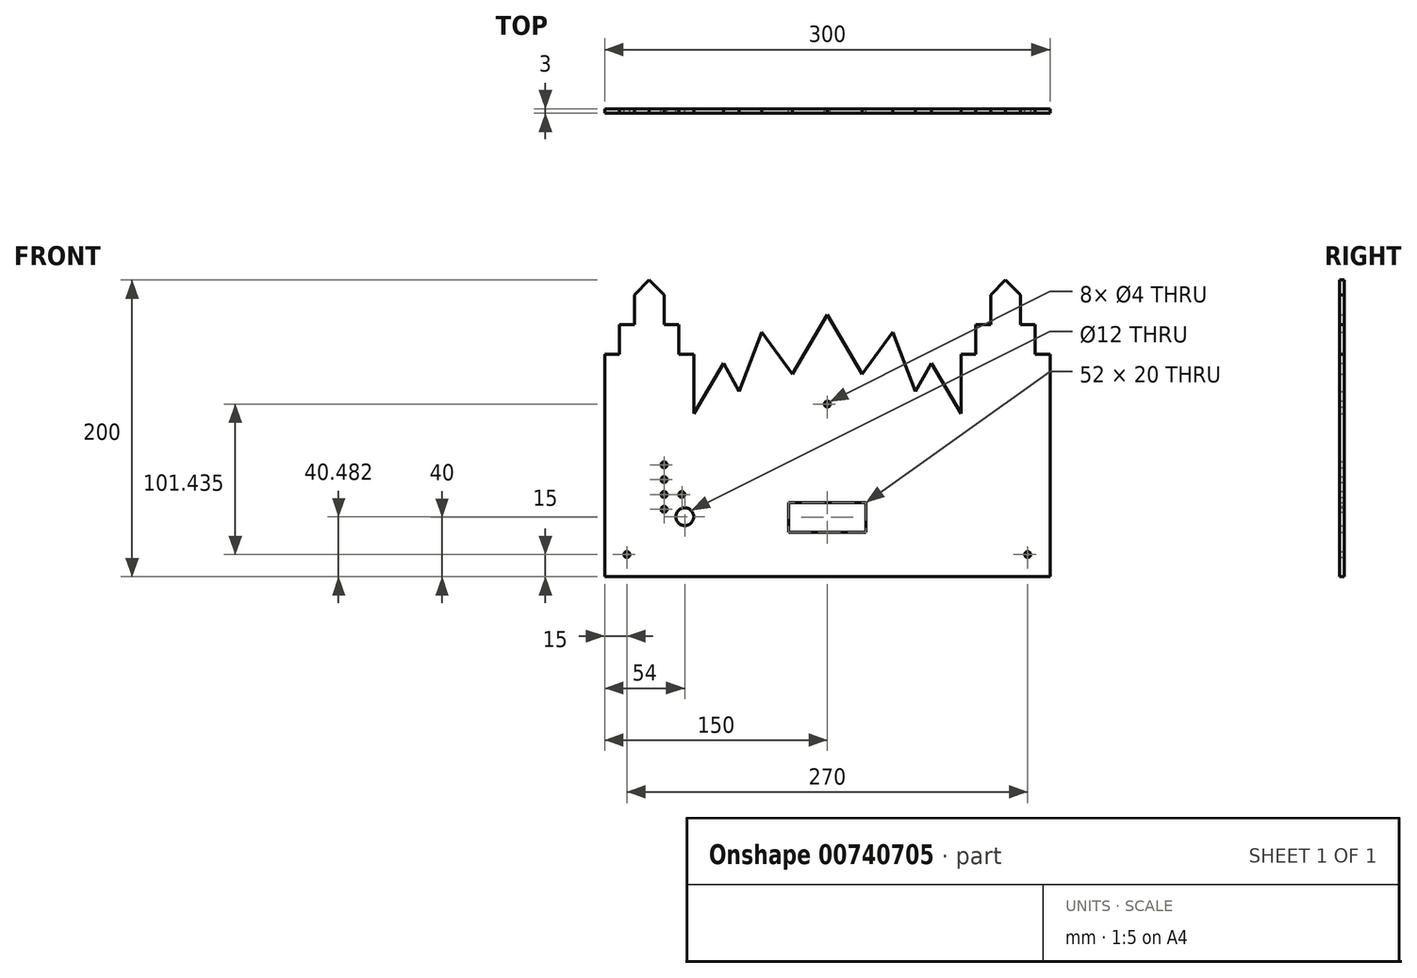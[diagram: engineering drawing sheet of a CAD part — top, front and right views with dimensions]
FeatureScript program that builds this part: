
annotation { "Feature Type Name" : "Feature", "Feature Type Description" : "" }
export const myFeature = defineFeature(function(context is Context, id is Id, definition is map)
    precondition{}
    {
        {
            var Q0;
            Q0=qCreatedBy(makeId("Front.planeOp"),FACE);
            var sketch = newSketch(context, id + "F0", { "sketchPlane" : qUnion([Q0])});
            skLineSegment(sketch, "E0", {"start": v(0, 0) * mm, "end": v(0, -200) * mm, "construction": true});
            skLineSegment(sketch, "E1", {"start": v(0, -200) * mm, "end": v(300, -200) * mm, "construction": true});
            skLineSegment(sketch, "E2", {"start": v(300, -200) * mm, "end": v(300, 0) * mm, "construction": true});
            skLineSegment(sketch, "E3", {"start": v(300, 0) * mm, "end": v(0, 0) * mm, "construction": true});
            skLineSegment(sketch, "E4", {"start": v(0, -200) * mm, "end": v(60, -200) * mm});
            skLineSegment(sketch, "E5", {"start": v(10, -50) * mm, "end": v(10, -30) * mm});
            skLineSegment(sketch, "E6", {"start": v(50, -50) * mm, "end": v(50, -30) * mm});
            skLineSegment(sketch, "E7", {"start": v(50, -30) * mm, "end": v(40, -30) * mm});
            skLineSegment(sketch, "E8", {"start": v(0, -50) * mm, "end": v(0, -200) * mm});
            skLineSegment(sketch, "E9", {"start": v(0, -50) * mm, "end": v(10, -50) * mm});
            skLineSegment(sketch, "E10", {"start": v(50, -50) * mm, "end": v(60, -50) * mm});
            skLineSegment(sketch, "E11", {"start": v(60, -90) * mm, "end": v(60, -50) * mm});
            skLineSegment(sketch, "E12", {"start": v(80, -56) * mm, "end": v(60, -90) * mm});
            skLineSegment(sketch, "E13", {"start": v(80, -56) * mm, "end": v(90.67, -75) * mm});
            skLineSegment(sketch, "E14", {"start": v(90.67, -75) * mm, "end": v(105.81, -35.1) * mm});
            skLineSegment(sketch, "E15", {"start": v(105.81, -35.1) * mm, "end": v(126.57, -63.45) * mm});
            skLineSegment(sketch, "E16", {"start": v(126.57, -63.45) * mm, "end": v(150, -23.47) * mm});
            skLineSegment(sketch, "E17", {"start": v(150, -170) * mm, "end": v(124, -170) * mm});
            skLineSegment(sketch, "E18", {"start": v(124, -170) * mm, "end": v(124, -150) * mm});
            skLineSegment(sketch, "E19", {"start": v(124, -150) * mm, "end": v(150, -150) * mm});
            skCircle(sketch, "E20", {"center": v(40, -124.52) * mm, "radius": 2 * mm});
            skCircle(sketch, "E21", {"center": v(40, -134.52) * mm, "radius": 2 * mm});
            skCircle(sketch, "E22", {"center": v(40, -144.52) * mm, "radius": 2 * mm});
            skCircle(sketch, "E23", {"center": v(40, -154.52) * mm, "radius": 2 * mm});
            skCircle(sketch, "E24", {"center": v(52, -144.52) * mm, "radius": 2 * mm});
            skLineSegment(sketch, "E25.MirrorCS", {"start": v(173.43, -63.45) * mm, "end": v(150, -23.47) * mm});
            skLineSegment(sketch, "E26.MirrorCS", {"start": v(209.33, -75) * mm, "end": v(194.19, -35.1) * mm});
            skLineSegment(sketch, "E27.MirrorCS", {"start": v(220, -56) * mm, "end": v(209.33, -75) * mm});
            skLineSegment(sketch, "E28.MirrorCS", {"start": v(220, -56) * mm, "end": v(240, -90) * mm});
            skLineSegment(sketch, "E29.MirrorCS", {"start": v(240, -90) * mm, "end": v(240, -50) * mm});
            skLineSegment(sketch, "E30.MirrorCS", {"start": v(250, -50) * mm, "end": v(240, -50) * mm});
            skLineSegment(sketch, "E31.MirrorCS", {"start": v(250, -50) * mm, "end": v(250, -30) * mm});
            skLineSegment(sketch, "E32.MirrorCS", {"start": v(250, -30) * mm, "end": v(260, -30) * mm});
            skLineSegment(sketch, "E33.MirrorCS", {"start": v(260, -30) * mm, "end": v(260, -10) * mm});
            skLineSegment(sketch, "E34.MirrorCS", {"start": v(260, -10) * mm, "end": v(270, 0) * mm});
            skLineSegment(sketch, "E35.MirrorCS", {"start": v(280, -10) * mm, "end": v(270, 0) * mm});
            skLineSegment(sketch, "E36.MirrorCS", {"start": v(280, -30) * mm, "end": v(280, -10) * mm});
            skLineSegment(sketch, "E37.MirrorCS", {"start": v(290, -30) * mm, "end": v(280, -30) * mm});
            skLineSegment(sketch, "E38.MirrorCS", {"start": v(300, -50) * mm, "end": v(290, -50) * mm});
            skLineSegment(sketch, "E39.MirrorCS", {"start": v(290, -50) * mm, "end": v(290, -30) * mm});
            skLineSegment(sketch, "E40", {"start": v(0, -200) * mm, "end": v(300, -200) * mm});
            skLineSegment(sketch, "E41", {"start": v(300, -50) * mm, "end": v(300, -200) * mm});
            skLineSegment(sketch, "E42.MirrorCS", {"start": v(176, -150) * mm, "end": v(150, -150) * mm});
            skLineSegment(sketch, "E43.MirrorCS", {"start": v(176, -170) * mm, "end": v(176, -150) * mm});
            skLineSegment(sketch, "E44.MirrorCS", {"start": v(150, -170) * mm, "end": v(176, -170) * mm});
            skPoint(sketch, "E45.start.orphan", {"position": v(150, -200) * mm});
            skPoint(sketch, "E46.trimOffspring.end.orphan", {"position": v(150, 0) * mm});
            skCircle(sketch, "E47", {"center": v(54, -159.52) * mm, "radius": 6 * mm});
            skCircle(sketch, "E48", {"center": v(15, -185) * mm, "radius": 2 * mm});
            skLineSegment(sketch, "E49", {"start": v(150, 0) * mm, "end": v(150, -200) * mm});
            skLineSegment(sketch, "E50", {"start": v(0, -200) * mm, "end": v(0, 0) * mm});
            skLineSegment(sketch, "E51.MirrorCS", {"start": v(10, -30) * mm, "end": v(20, -30) * mm});
            skLineSegment(sketch, "E52.MirrorCS", {"start": v(20, -30) * mm, "end": v(20, -10) * mm});
            skLineSegment(sketch, "E53.MirrorCS", {"start": v(20, -10) * mm, "end": v(30, 0) * mm});
            skLineSegment(sketch, "E54.MirrorCS", {"start": v(40, -10) * mm, "end": v(30, 0) * mm});
            skLineSegment(sketch, "E55.MirrorCS", {"start": v(40, -30) * mm, "end": v(40, -10) * mm});
            skCircle(sketch, "E56", {"center": v(150, -83.56) * mm, "radius": 2 * mm});
            skLineSegment(sketch, "E57.MirrorCS", {"start": v(194.19, -35.1) * mm, "end": v(173.43, -63.45) * mm});
            skCircle(sketch, "E58.MirrorC", {"center": v(285, -185) * mm, "radius": 2 * mm});
            skSolve(sketch);
        }
        {
            var Q0;
            Q0=makeQuery(id+"F0.imprint","IMPRINT",FACE,{"disambiguationData":[TD([[makeQuery(id+"F0.imprint","IMPRINT",EDGE,{"derivedFrom":sQuery(id+"F0.wireOp",EDGE,"E5")}),-1.0]])]});
            var Q1;
            {var subQ8=sQuery(id+"F0.wireOp",EDGE,"E25.MirrorCS");Q1=makeQuery(id+"F0.imprint","IMPRINT",FACE,{"disambiguationData":[TD([[makeQuery(id+"F0.imprint","IMPRINT",EDGE,{"derivedFrom":subQ8}),1.0]])]});}
            extrude(context, id + "F1", {"entities" : qUnion([Q0, Q1]), "depth" : 3 * mm, "offsetDistance" : 25 * mm});
        }
    });
